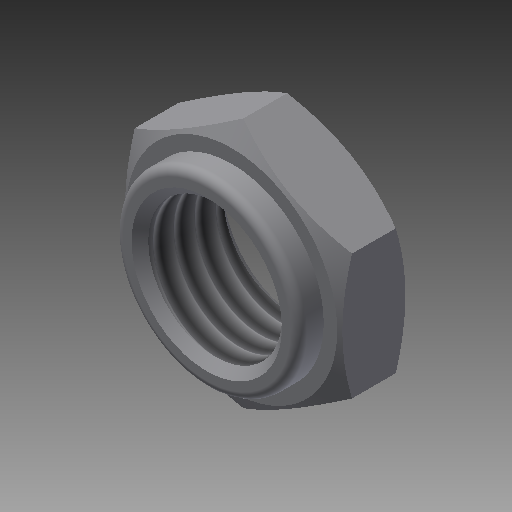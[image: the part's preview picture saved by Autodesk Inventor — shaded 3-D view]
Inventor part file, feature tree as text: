
AUTODESK INVENTOR PART (.ipt)
format: ipt  version: 2019 (Build 230136000, 136)  size: 183,296 bytes
history: native  units: mm
features: extrude x2, sketch x2, other x2, hole x1, thread x1, chamfer x1, revolve x1, fillet x1
ambient origin geometry x8: Origin, YZ Plane, XZ Plane, XY Plane, X Axis, Y Axis, Z Axis, Center Point
bodies: Solido1 (feature_tree)
feature tree (11):
  extrude  "Estrusione1"  Depth=13.0mm
  extrude  "Estrusione2"  Depth=4.0mm TaperAngle=0.0deg
  sketch  "Schizzo3"
  other  "Piano di lavoro1"
  hole  "Foro1"  [1 undecoded]
  thread  "Filettatura1"
  chamfer  "Smusso1"  Distance=11.0mm
  revolve  "Rivoluzione2"
  fillet  "Raccordo1"  [1 undecoded]
  sketch  "Schizzo1"
  other  "Linea chiusa proiettata1"
note: 2 required parameter values undecoded (feature->parameter linkage not recoverable at this tier; creation-order binding heuristic only, values carry confidence <= 0.55)
